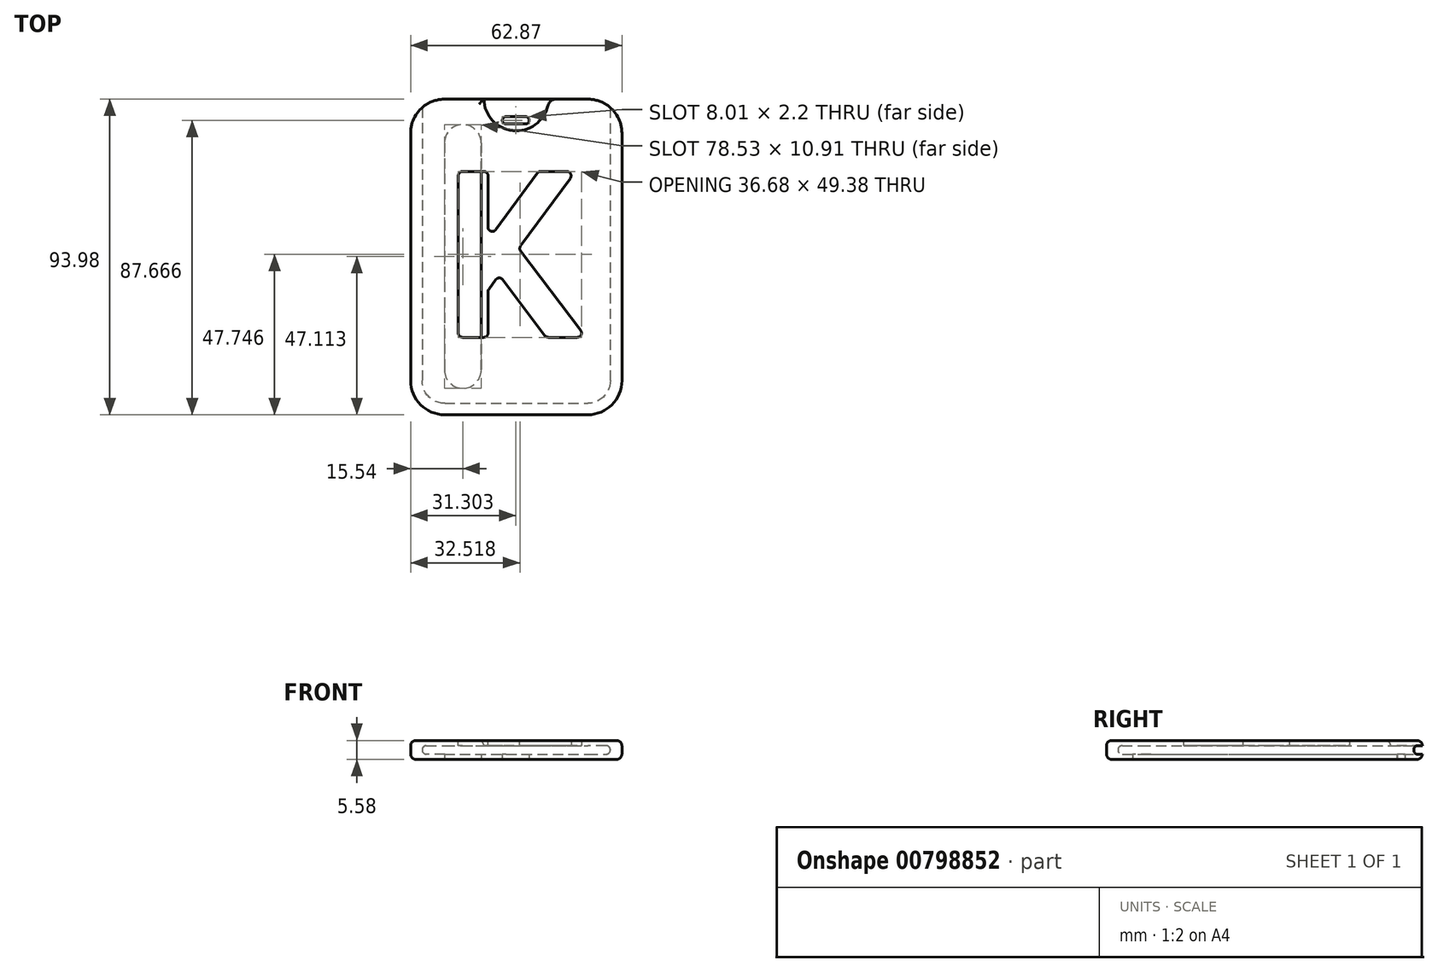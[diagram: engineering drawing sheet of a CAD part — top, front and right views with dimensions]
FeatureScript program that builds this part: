
annotation { "Feature Type Name" : "Feature", "Feature Type Description" : "" }
export const myFeature = defineFeature(function(context is Context, id is Id, definition is map)
    precondition{}
    {
        {
            var Q0;
            Q0=qCreatedBy(makeId("Top.planeOp"),FACE);
            var sketch = newSketch(context, id + "F0", { "sketchPlane" : qUnion([Q0])});
            skLineSegment(sketch, "E0.bottom", {"start": v(-29.09, 36.7) * mm, "end": v(13.46, 36.7) * mm, "construction": true});
            skLineSegment(sketch, "E0.top", {"start": v(-29.09, -49.66) * mm, "end": v(13.46, -49.66) * mm, "construction": true});
            skLineSegment(sketch, "E0.left", {"start": v(-35.44, 30.35) * mm, "end": v(-35.44, -43.31) * mm, "construction": true});
            skLineSegment(sketch, "E0.right", {"start": v(19.8, 30.35) * mm, "end": v(19.8, -43.31) * mm, "construction": true});
            skPoint(sketch, "E1.visualSharp", {"position": v(-35.44, 36.7) * mm});
            skArc(sketch, "E1.filletArc", {"start": v(-29.09, 36.7) * mm, "mid": v(-33.58, 34.84) * mm, "end": v(-35.44, 30.35) * mm, "construction": true});
            skPoint(sketch, "E2.visualSharp", {"position": v(19.8, 36.7) * mm});
            skArc(sketch, "E2.filletArc", {"start": v(19.8, 30.35) * mm, "mid": v(17.95, 34.84) * mm, "end": v(13.46, 36.7) * mm, "construction": true});
            skPoint(sketch, "E3.visualSharp", {"position": v(19.8, -49.66) * mm});
            skArc(sketch, "E3.filletArc", {"start": v(13.46, -49.66) * mm, "mid": v(17.95, -47.8) * mm, "end": v(19.8, -43.31) * mm, "construction": true});
            skPoint(sketch, "E4.visualSharp", {"position": v(-35.44, -49.66) * mm});
            skArc(sketch, "E4.filletArc", {"start": v(-35.44, -43.31) * mm, "mid": v(-33.58, -47.8) * mm, "end": v(-29.09, -49.66) * mm, "construction": true});
            skArc(sketch, "E5.0", {"start": v(-29.09, 40.5) * mm, "mid": v(-36.27, 37.53) * mm, "end": v(-39.25, 30.35) * mm});
            skLineSegment(sketch, "E5.1", {"start": v(-29.09, 40.5) * mm, "end": v(13.46, 40.5) * mm});
            skLineSegment(sketch, "E5.2", {"start": v(-39.25, 30.35) * mm, "end": v(-39.25, -43.31) * mm});
            skArc(sketch, "E5.3", {"start": v(23.62, 30.35) * mm, "mid": v(20.64, 37.53) * mm, "end": v(13.46, 40.5) * mm});
            skArc(sketch, "E5.4", {"start": v(-39.25, -43.31) * mm, "mid": v(-36.27, -50.5) * mm, "end": v(-29.09, -53.47) * mm});
            skLineSegment(sketch, "E5.5", {"start": v(-29.09, -53.47) * mm, "end": v(13.46, -53.47) * mm});
            skArc(sketch, "E5.6", {"start": v(13.46, -53.47) * mm, "mid": v(20.64, -50.5) * mm, "end": v(23.62, -43.31) * mm});
            skLineSegment(sketch, "E5.7", {"start": v(23.62, 30.35) * mm, "end": v(23.62, -43.31) * mm});
            skArc(sketch, "E6.0", {"start": v(20.19, 30.35) * mm, "mid": v(18.22, 35.1) * mm, "end": v(13.46, 37.08) * mm});
            skLineSegment(sketch, "E6.1", {"start": v(-29.09, 37.08) * mm, "end": v(13.46, 37.08) * mm});
            skLineSegment(sketch, "E6.2", {"start": v(20.19, 30.35) * mm, "end": v(20.19, -43.31) * mm});
            skArc(sketch, "E6.3", {"start": v(-29.09, 37.08) * mm, "mid": v(-33.85, 35.1) * mm, "end": v(-35.82, 30.35) * mm});
            skArc(sketch, "E6.4", {"start": v(13.46, -50.04) * mm, "mid": v(18.22, -48.07) * mm, "end": v(20.19, -43.31) * mm});
            skLineSegment(sketch, "E6.5", {"start": v(-29.09, -50.04) * mm, "end": v(13.46, -50.04) * mm});
            skArc(sketch, "E6.6", {"start": v(-35.82, -43.31) * mm, "mid": v(-33.85, -48.07) * mm, "end": v(-29.09, -50.04) * mm});
            skLineSegment(sketch, "E6.7", {"start": v(-35.82, 30.35) * mm, "end": v(-35.82, -43.31) * mm});
            skLineSegment(sketch, "E7", {"start": v(-35.82, 30.35) * mm, "end": v(-35.82, 37.96) * mm});
            skLineSegment(sketch, "E8", {"start": v(-7.82, 40.5) * mm, "end": v(-7.82, 48.78) * mm, "construction": true});
            skLineSegment(sketch, "E9.MirrorCS", {"start": v(20.19, 30.35) * mm, "end": v(20.19, 37.96) * mm});
            skSolve(sketch);
        }
        {
            var Q0;
            {var subQ0=sQuery(id+"F0.wireOp",EDGE,"E5.1");Q0=makeQuery(id+"F0.imprint","IMPRINT",FACE,{"disambiguationData":[TD([[makeQuery(id+"F0.imprint","IMPRINT",EDGE,{"derivedFrom":subQ0}),-1.0]])]});}
            var Q1;
            Q1=makeQuery(id+"F0.imprint","IMPRINT",FACE,{"disambiguationData":[TD([[makeQuery(id+"F0.imprint","IMPRINT",EDGE,{"derivedFrom":sQuery(id+"F0.wireOp",EDGE,"E6.0")}),1.0]])]});
            var Q2;
            {var subQ1=sQuery(id+"F0.wireOp",EDGE,"E5.2");Q2=makeQuery(id+"F0.imprint","IMPRINT",FACE,{"disambiguationData":[TD([[makeQuery(id+"F0.imprint","IMPRINT",EDGE,{"derivedFrom":subQ1}),1.0]])]});}
            extrude(context, id + "F1", {"entities" : qUnion([Q0, Q1, Q2]), "endBound" : BoundingType.SYMMETRIC, "depth" : 5.6 * mm, "offsetDistance" : 25.4 * mm});
        }
        {
            var Q0;
            {var subQ0=sQuery(id+"F0.wireOp",EDGE,"E5.1");Q0=makeQuery(id+"F0.imprint","IMPRINT",FACE,{"disambiguationData":[TD([[makeQuery(id+"F0.imprint","IMPRINT",EDGE,{"derivedFrom":subQ0}),-1.0]])]});}
            var Q1;
            Q1=makeQuery(id+"F0.imprint","IMPRINT",FACE,{"disambiguationData":[TD([[makeQuery(id+"F0.imprint","IMPRINT",EDGE,{"derivedFrom":sQuery(id+"F0.wireOp",EDGE,"E6.0")}),1.0]])]});
            extrude(context, id + "F2", {"entities" : qUnion([Q0, Q1]), "operationType" : NewBodyOperationType.REMOVE, "endBound" : BoundingType.SYMMETRIC, "depth" : 2.54 * mm, "offsetDistance" : 25.4 * mm});
        }
        {
            var Q0;
            Q0=makeQuery(id+"F1.opExtrude","CAP_FACE",FACE,{"disambiguationData":[OSD([sQuery(id+"F0.wireOp",EDGE,"E5.0"),sQuery(id+"F0.wireOp",EDGE,"E5.1"),sQuery(id+"F0.wireOp",EDGE,"E5.2"),sQuery(id+"F0.wireOp",EDGE,"E5.3"),sQuery(id+"F0.wireOp",EDGE,"E5.4"),sQuery(id+"F0.wireOp",EDGE,"E5.5"),sQuery(id+"F0.wireOp",EDGE,"E5.6"),sQuery(id+"F0.wireOp",EDGE,"E5.7")])],"isStart":false});
            var sketch = newSketch(context, id + "F3", { "sketchPlane" : qUnion([Q0])});
            skLineSegment(sketch, "E10.bottom", {"start": v(-25.07, 18.97) * mm, "end": v(-16.2, 18.97) * mm});
            skLineSegment(sketch, "E10.top", {"start": v(-25.07, -30.41) * mm, "end": v(-16.2, -30.41) * mm});
            skLineSegment(sketch, "E10.left", {"start": v(-25.07, 18.97) * mm, "end": v(-25.07, -30.41) * mm});
            skLineSegment(sketch, "E10.right", {"start": v(-16.2, 18.97) * mm, "end": v(-16.2, -1.51) * mm});
            skLineSegment(sketch, "E11", {"start": v(-16.2, -1.51) * mm, "end": v(-1.18, 18.97) * mm});
            skLineSegment(sketch, "E12", {"start": v(-1.18, 18.97) * mm, "end": v(9.74, 18.97) * mm});
            skLineSegment(sketch, "E13", {"start": v(9.74, 18.97) * mm, "end": v(-7.08, -3.97) * mm});
            skLineSegment(sketch, "E14", {"start": v(-7.08, -3.97) * mm, "end": v(12.9, -30.41) * mm});
            skLineSegment(sketch, "E15", {"start": v(12.9, -30.41) * mm, "end": v(1.13, -30.41) * mm});
            skLineSegment(sketch, "E16", {"start": v(1.13, -30.41) * mm, "end": v(-12.88, -11.88) * mm});
            skLineSegment(sketch, "E17.trimOffspring", {"start": v(-12.88, -11.88) * mm, "end": v(-16.2, -16.4) * mm});
            skLineSegment(sketch, "E18.trimOffspring", {"start": v(-16.2, -16.4) * mm, "end": v(-16.2, -30.41) * mm});
            skSolve(sketch);
        }
        {
            var Q0;
            Q0=makeQuery(id+"F3.imprint","IMPRINT",FACE,{"disambiguationData":[TD([[makeQuery(id+"F3.imprint","IMPRINT",EDGE,{"derivedFrom":sQuery(id+"F3.wireOp",EDGE,"E10.bottom")}),-1.0]])]});
            var Q1;
            Q1=sQuery(id+"F3.wireOp",EDGE,"E10.right");
            var Q2;
            Q2=sQuery(id+"F3.wireOp",EDGE,"E10.bottom");
            var Q3;
            Q3=sQuery(id+"F3.wireOp",EDGE,"E10.left");
            var Q4;
            Q4=sQuery(id+"F3.wireOp",EDGE,"E11");
            var Q5;
            Q5=sQuery(id+"F3.wireOp",EDGE,"E12");
            var Q6;
            Q6=sQuery(id+"F3.wireOp",EDGE,"E13");
            var Q7;
            Q7=sQuery(id+"F3.wireOp",EDGE,"E14");
            var Q8;
            Q8=sQuery(id+"F3.wireOp",EDGE,"E15");
            var Q9;
            Q9=sQuery(id+"F3.wireOp",EDGE,"E16");
            var Q10;
            Q10=sQuery(id+"F3.wireOp",EDGE,"E17.trimOffspring");
            var Q11;
            Q11=sQuery(id+"F3.wireOp",EDGE,"E18.trimOffspring");
            var Q12;
            Q12=sQuery(id+"F3.wireOp",EDGE,"E10.top");
            extrude(context, id + "F4", {"entities" : qUnion([Q0]), "operationType" : NewBodyOperationType.REMOVE, "surfaceEntities" : qUnion([Q1, Q2, Q3, Q4, Q5, Q6, Q7, Q8, Q9, Q10, Q11, Q12]), "oppositeDirection" : true, "depth" : 2.54 * mm, "offsetDistance" : 25.4 * mm});
        }
        {
            var Q0;
            Q0=makeQuery(id+"F1.opExtrude","CAP_FACE",FACE,{"disambiguationData":[OSD([sQuery(id+"F0.wireOp",EDGE,"E5.0"),sQuery(id+"F0.wireOp",EDGE,"E5.1"),sQuery(id+"F0.wireOp",EDGE,"E5.2"),sQuery(id+"F0.wireOp",EDGE,"E5.3"),sQuery(id+"F0.wireOp",EDGE,"E5.4"),sQuery(id+"F0.wireOp",EDGE,"E5.5"),sQuery(id+"F0.wireOp",EDGE,"E5.6"),sQuery(id+"F0.wireOp",EDGE,"E5.7")])],"isStart":true});
            var sketch = newSketch(context, id + "F5", { "sketchPlane" : qUnion([Q0])});
            skLineSegment(sketch, "E19.left", {"start": v(-29.16, -27.45) * mm, "end": v(-29.16, 40.17) * mm});
            skLineSegment(sketch, "E19.right", {"start": v(-18.26, -27.45) * mm, "end": v(-18.26, 40.17) * mm});
            skArc(sketch, "E20", {"start": v(-29.16, -27.45) * mm, "mid": v(-23.7, -32.9) * mm, "end": v(-18.26, -27.45) * mm});
            skArc(sketch, "E21", {"start": v(-29.16, 40.17) * mm, "mid": v(-23.7, 45.62) * mm, "end": v(-18.26, 40.17) * mm});
            skLineSegment(sketch, "E22.bottom", {"start": v(-5.05, -33.1) * mm, "end": v(-10.85, -33.1) * mm});
            skLineSegment(sketch, "E22.top", {"start": v(-5.05, -35.3) * mm, "end": v(-10.85, -35.3) * mm});
            skArc(sketch, "E23", {"start": v(-5.05, -35.3) * mm, "mid": v(-3.94, -34.2) * mm, "end": v(-5.05, -33.1) * mm});
            skArc(sketch, "E24", {"start": v(-10.85, -35.3) * mm, "mid": v(-11.95, -34.2) * mm, "end": v(-10.85, -33.1) * mm});
            skSolve(sketch);
        }
        {
            var Q0;
            Q0=makeQuery(id+"F5.imprint","IMPRINT",FACE,{"disambiguationData":[TD([[makeQuery(id+"F5.imprint","IMPRINT",EDGE,{"derivedFrom":sQuery(id+"F5.wireOp",EDGE,"E19.left")}),-1.0]])]});
            var Q1;
            Q1=makeQuery(id+"F5.imprint","IMPRINT",FACE,{"disambiguationData":[TD([[makeQuery(id+"F5.imprint","IMPRINT",EDGE,{"derivedFrom":sQuery(id+"F5.wireOp",EDGE,"E22.bottom")}),1.0]])]});
            extrude(context, id + "F6", {"entities" : qUnion([Q0, Q1]), "operationType" : NewBodyOperationType.REMOVE, "oppositeDirection" : true, "depth" : 2.54 * mm, "offsetDistance" : 25.4 * mm});
        }
        {
            var Q0;
            Q0=makeQuery(id+"F3.imprint","IMPRINT",FACE,{"disambiguationData":[TD([[makeQuery(id+"F3.imprint","IMPRINT",EDGE,{"derivedFrom":sQuery(id+"F3.wireOp",EDGE,"E10.bottom")}),1.0]])]});
            var sketch = newSketch(context, id + "F7", { "sketchPlane" : qUnion([Q0])});
            skCircle(sketch, "E25", {"center": v(-7.8, 40.74) * mm, "radius": 9.66 * mm});
            skSolve(sketch);
        }
        {
            var Q0;
            {var subQ0=sQuery(id+"F7.wireOp",EDGE,"E25");var subQ1=makeQuery(id+"F3.imprint","IMPRINT",EDGE,{"derivedFrom":makeQuery(id+"F1.opExtrude","CAP_EDGE",EDGE,{"disambiguationData":[OSD([sQuery(id+"F0.wireOp",EDGE,"E5.1")])],"isStart":false})});var subQ2=makeQuery(id+"F7.imprint","INTERSECT",VERTEX,{"disambiguationData":[OD(0.0)],"derivedFrom":[subQ1,subQ0]});Q0=makeQuery(id+"F7.imprint","IMPRINT",FACE,{"disambiguationData":[TD([[makeQuery(id+"F7.imprint","IMPRINT",EDGE,{"disambiguationData":[TD([[subQ2,-1.0]])],"derivedFrom":subQ0}),1.0]])]});}
            extrude(context, id + "F8", {"entities" : qUnion([Q0]), "operationType" : NewBodyOperationType.REMOVE, "oppositeDirection" : true, "depth" : 2.54 * mm, "offsetDistance" : 25.4 * mm});
        }
        {
            var Q0;
            {var subQ0=sQuery(id+"F7.wireOp",EDGE,"E25");var subQ1=sQuery(id+"F0.wireOp",EDGE,"E5.1");Q0=makeQuery(id+"F8.boolean.opBoolean","COPY",EDGE,{"derivedFrom":makeQuery(id+"F8.opExtrude","SWEPT_EDGE",EDGE,{"disambiguationData":[OSD([subQ1,subQ0]),TDD([makeQuery(id+"F7.imprint","INTERSECT",VERTEX,{"disambiguationData":[OD(1.0)],"derivedFrom":[makeQuery(id+"F3.imprint","IMPRINT",EDGE,{"derivedFrom":makeQuery(id+"F1.opExtrude","CAP_EDGE",EDGE,{"disambiguationData":[OSD([subQ1])],"isStart":false})}),subQ0]})])]})});}
            var Q1;
            {var subQ0=sQuery(id+"F7.wireOp",EDGE,"E25");var subQ1=sQuery(id+"F0.wireOp",EDGE,"E5.1");Q1=makeQuery(id+"F8.boolean.opBoolean","COPY",EDGE,{"derivedFrom":makeQuery(id+"F8.opExtrude","SWEPT_EDGE",EDGE,{"disambiguationData":[OSD([subQ1,subQ0]),TDD([makeQuery(id+"F7.imprint","INTERSECT",VERTEX,{"disambiguationData":[OD(0.0)],"derivedFrom":[makeQuery(id+"F3.imprint","IMPRINT",EDGE,{"derivedFrom":makeQuery(id+"F1.opExtrude","CAP_EDGE",EDGE,{"disambiguationData":[OSD([subQ1])],"isStart":false})}),subQ0]})])]})});}
            fillet(context, id + "F9", {"entities" : qUnion([Q0, Q1]), "radius" : 2.54 * mm, "tangentPropagation" : true, "allowEdgeOverflow" : false});
        }
        {
            var Q0;
            Q0=makeQuery(id+"F1.opExtrude","CAP_EDGE",EDGE,{"disambiguationData":[OSD([sQuery(id+"F0.wireOp",EDGE,"E5.2")])],"isStart":false});
            var Q1;
            Q1=makeQuery(id+"F1.opExtrude","CAP_EDGE",EDGE,{"disambiguationData":[OSD([sQuery(id+"F0.wireOp",EDGE,"E5.2")])],"isStart":true});
            var Q2;
            Q2=makeQuery(id+"F6.boolean.opBoolean","COPY",EDGE,{"derivedFrom":makeQuery(id+"F6.opExtrude","CAP_EDGE",EDGE,{"disambiguationData":[OSD([sQuery(id+"F5.wireOp",EDGE,"E19.left")])],"isStart":true})});
            fillet(context, id + "F10", {"entities" : qUnion([Q0, Q1, Q2]), "radius" : 1.52 * mm, "tangentPropagation" : true, "allowEdgeOverflow" : false});
        }
        {
            var Q0;
            Q0=makeQuery(id+"F4.boolean.opBoolean","COPY",EDGE,{"derivedFrom":makeQuery(id+"F4.opExtrude","SWEPT_EDGE",EDGE,{"disambiguationData":[OSD([sQuery(id+"F3.wireOp",EDGE,"E12"),sQuery(id+"F3.wireOp",EDGE,"E13")])]})});
            var Q1;
            Q1=makeQuery(id+"F4.boolean.opBoolean","COPY",EDGE,{"derivedFrom":makeQuery(id+"F4.opExtrude","SWEPT_EDGE",EDGE,{"disambiguationData":[OSD([sQuery(id+"F3.wireOp",EDGE,"E11"),sQuery(id+"F3.wireOp",EDGE,"E12")])]})});
            var Q2;
            Q2=makeQuery(id+"F4.boolean.opBoolean","COPY",EDGE,{"derivedFrom":makeQuery(id+"F4.opExtrude","SWEPT_EDGE",EDGE,{"disambiguationData":[OSD([sQuery(id+"F3.wireOp",EDGE,"E10.bottom"),sQuery(id+"F3.wireOp",EDGE,"E10.right")])]})});
            var Q3;
            Q3=makeQuery(id+"F4.boolean.opBoolean","COPY",EDGE,{"derivedFrom":makeQuery(id+"F4.opExtrude","SWEPT_EDGE",EDGE,{"disambiguationData":[OSD([sQuery(id+"F3.wireOp",EDGE,"E10.right"),sQuery(id+"F3.wireOp",EDGE,"E11")])]})});
            var Q4;
            Q4=makeQuery(id+"F4.boolean.opBoolean","COPY",EDGE,{"derivedFrom":makeQuery(id+"F4.opExtrude","SWEPT_EDGE",EDGE,{"disambiguationData":[OSD([sQuery(id+"F3.wireOp",EDGE,"E13"),sQuery(id+"F3.wireOp",EDGE,"E14")])]})});
            var Q5;
            Q5=makeQuery(id+"F4.boolean.opBoolean","COPY",EDGE,{"derivedFrom":makeQuery(id+"F4.opExtrude","SWEPT_EDGE",EDGE,{"disambiguationData":[OSD([sQuery(id+"F3.wireOp",EDGE,"E14"),sQuery(id+"F3.wireOp",EDGE,"E15")])]})});
            var Q6;
            Q6=makeQuery(id+"F4.boolean.opBoolean","COPY",EDGE,{"derivedFrom":makeQuery(id+"F4.opExtrude","SWEPT_EDGE",EDGE,{"disambiguationData":[OSD([sQuery(id+"F3.wireOp",EDGE,"E15"),sQuery(id+"F3.wireOp",EDGE,"E16")])]})});
            var Q7;
            Q7=makeQuery(id+"F4.boolean.opBoolean","COPY",EDGE,{"derivedFrom":makeQuery(id+"F4.opExtrude","SWEPT_EDGE",EDGE,{"disambiguationData":[OSD([sQuery(id+"F3.wireOp",EDGE,"E16"),sQuery(id+"F3.wireOp",EDGE,"E17.trimOffspring")])]})});
            var Q8;
            Q8=makeQuery(id+"F4.boolean.opBoolean","COPY",EDGE,{"derivedFrom":makeQuery(id+"F4.opExtrude","SWEPT_EDGE",EDGE,{"disambiguationData":[OSD([sQuery(id+"F3.wireOp",EDGE,"E17.trimOffspring"),sQuery(id+"F3.wireOp",EDGE,"E18.trimOffspring")])]})});
            var Q9;
            Q9=makeQuery(id+"F4.boolean.opBoolean","COPY",EDGE,{"derivedFrom":makeQuery(id+"F4.opExtrude","SWEPT_EDGE",EDGE,{"disambiguationData":[OSD([sQuery(id+"F3.wireOp",EDGE,"E10.top"),sQuery(id+"F3.wireOp",EDGE,"E18.trimOffspring")])]})});
            var Q10;
            Q10=makeQuery(id+"F4.boolean.opBoolean","COPY",EDGE,{"derivedFrom":makeQuery(id+"F4.opExtrude","SWEPT_EDGE",EDGE,{"disambiguationData":[OSD([sQuery(id+"F3.wireOp",EDGE,"E10.top"),sQuery(id+"F3.wireOp",EDGE,"E10.left")])]})});
            var Q11;
            Q11=makeQuery(id+"F4.boolean.opBoolean","COPY",EDGE,{"derivedFrom":makeQuery(id+"F4.opExtrude","SWEPT_EDGE",EDGE,{"disambiguationData":[OSD([sQuery(id+"F3.wireOp",EDGE,"E10.bottom"),sQuery(id+"F3.wireOp",EDGE,"E10.left")])]})});
            fillet(context, id + "F11", {"entities" : qUnion([Q0, Q1, Q2, Q3, Q4, Q5, Q6, Q7, Q8, Q9, Q10, Q11]), "radius" : 1.27 * mm, "tangentPropagation" : true, "allowEdgeOverflow" : false});
        }
        {
            var Q0;
            Q0=makeQuery(id+"F2.boolean.opBoolean","COPY",EDGE,{"derivedFrom":makeQuery(id+"F2.opExtrude","CAP_EDGE",EDGE,{"disambiguationData":[OSD([sQuery(id+"F0.wireOp",EDGE,"E6.7"),sQuery(id+"F0.wireOp",EDGE,"E7")])],"isStart":false})});
            var Q1;
            Q1=makeQuery(id+"F2.boolean.opBoolean","COPY",EDGE,{"derivedFrom":makeQuery(id+"F2.opExtrude","CAP_EDGE",EDGE,{"disambiguationData":[OSD([sQuery(id+"F0.wireOp",EDGE,"E6.7"),sQuery(id+"F0.wireOp",EDGE,"E7")])],"isStart":true})});
            fillet(context, id + "F12", {"entities" : qUnion([Q0, Q1]), "radius" : 1.27 * mm, "tangentPropagation" : true, "allowEdgeOverflow" : false});
        }
    });
